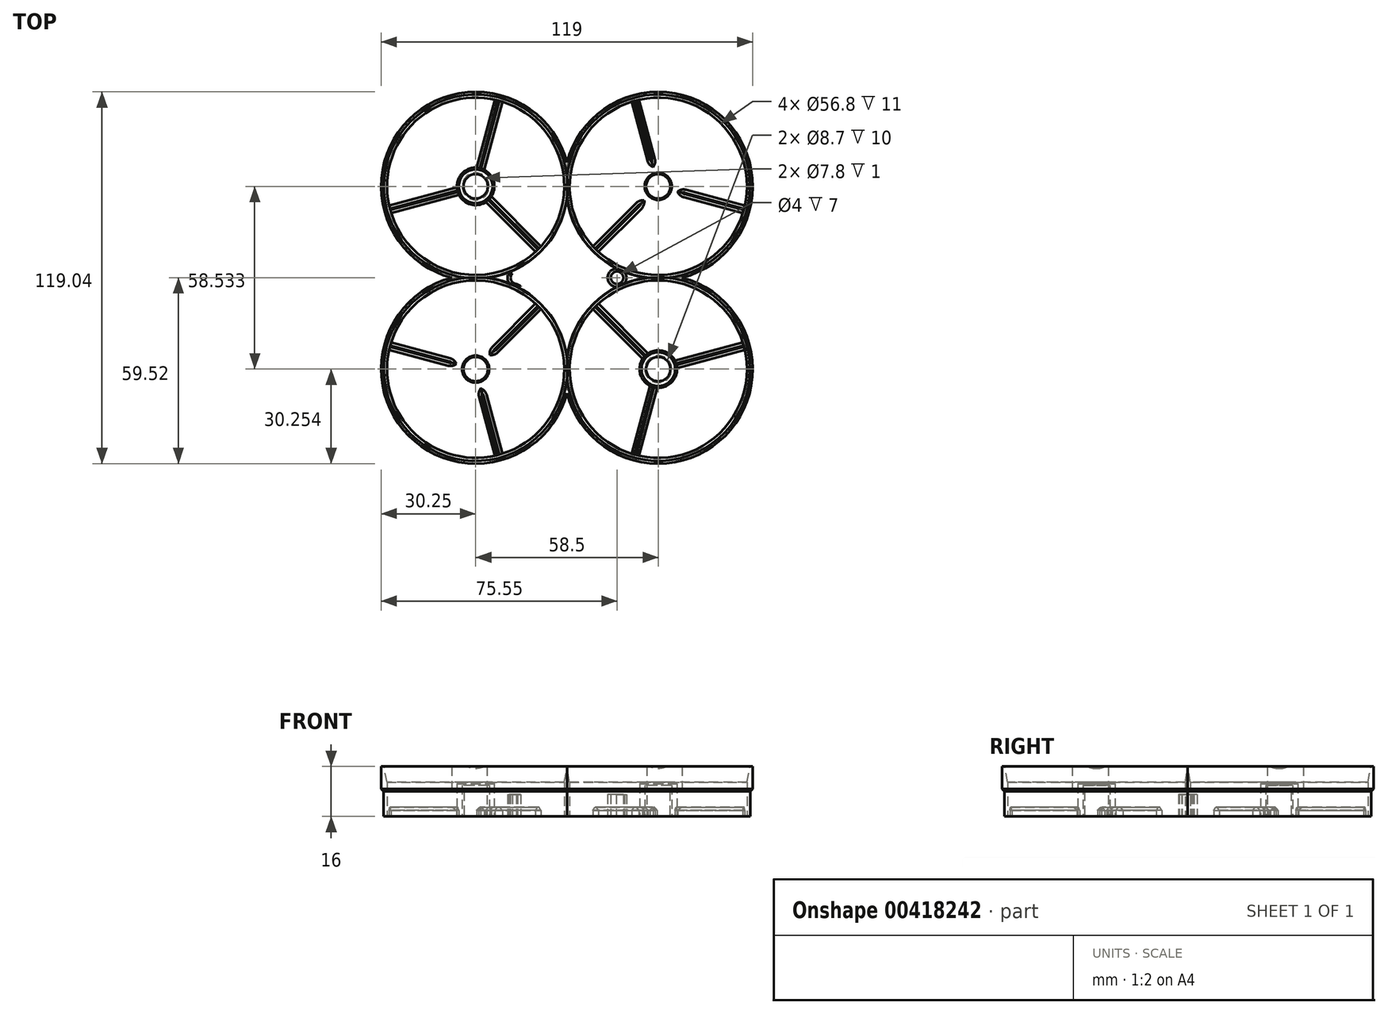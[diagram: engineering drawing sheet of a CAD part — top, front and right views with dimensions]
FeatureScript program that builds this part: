
annotation { "Feature Type Name" : "Feature", "Feature Type Description" : "" }
export const myFeature = defineFeature(function(context is Context, id is Id, definition is map)
    precondition{}
    {
        {
            var Q0;
            Q0=qCreatedBy(makeId("Top.planeOp"),FACE);
            var sketch = newSketch(context, id + "F0", { "sketchPlane" : qUnion([Q0])});
            skPoint(sketch, "E0.middle", {"position": v(0, 0) * mm});
            skCircle(sketch, "E1", {"center": v(-29.25, 29.27) * mm, "radius": 28.4 * mm});
            skArc(sketch, "E2", {"start": v(0, 33.1) * mm, "mid": v(-50.16, 50.08) * mm, "end": v(-32.96, 0) * mm});
            skArc(sketch, "E3.MirrorC", {"start": v(0, 33.1) * mm, "mid": v(50.16, 50.08) * mm, "end": v(32.96, 0) * mm});
            skCircle(sketch, "E4.MirrorC", {"center": v(29.25, 29.27) * mm, "radius": 28.4 * mm});
            skArc(sketch, "E5.MirrorC", {"start": v(0, -33.1) * mm, "mid": v(-50.16, -50.08) * mm, "end": v(-32.96, 0) * mm});
            skCircle(sketch, "E6.MirrorC", {"center": v(-29.25, -29.27) * mm, "radius": 28.4 * mm});
            skArc(sketch, "E7.MirrorC", {"start": v(0, -33.1) * mm, "mid": v(50.16, -50.08) * mm, "end": v(32.96, 0) * mm});
            skCircle(sketch, "E8.MirrorC", {"center": v(29.25, -29.27) * mm, "radius": 28.4 * mm});
            skArc(sketch, "E9.trimOffspring", {"start": v(-25.54, 0) * mm, "mid": v(-8.44, -8.36) * mm, "end": v(0, -25.43) * mm});
            skArc(sketch, "E10.trimOffspring", {"start": v(-25.54, 0) * mm, "mid": v(-8.44, 8.36) * mm, "end": v(0, 25.43) * mm});
            skArc(sketch, "E11.trimOffspring", {"start": v(25.54, 0) * mm, "mid": v(8.44, -8.36) * mm, "end": v(0, -25.43) * mm});
            skArc(sketch, "E12.trimOffspring", {"start": v(25.54, 0) * mm, "mid": v(8.44, 8.36) * mm, "end": v(0, 25.43) * mm});
            skArc(sketch, "E13", {"start": v(-21.6, 0) * mm, "mid": v(-7.88, 7.85) * mm, "end": v(0, 21.55) * mm});
            skArc(sketch, "E14.MirrorC", {"start": v(21.6, 0) * mm, "mid": v(7.88, 7.85) * mm, "end": v(0, 21.55) * mm});
            skArc(sketch, "E15.MirrorC", {"start": v(-21.6, 0) * mm, "mid": v(-7.88, -7.85) * mm, "end": v(0, -21.55) * mm});
            skArc(sketch, "E16.MirrorC", {"start": v(21.6, 0) * mm, "mid": v(7.88, -7.85) * mm, "end": v(0, -21.55) * mm});
            skArc(sketch, "E17.trimOffspring", {"start": v(0, 36.98) * mm, "mid": v(50.66, 50.63) * mm, "end": v(36.9, 0) * mm});
            skArc(sketch, "E18.trimOffspring", {"start": v(0, 36.98) * mm, "mid": v(-50.66, 50.63) * mm, "end": v(-36.9, 0) * mm});
            skArc(sketch, "E19.trimOffspring", {"start": v(0, -36.98) * mm, "mid": v(50.66, -50.63) * mm, "end": v(36.9, 0) * mm});
            skArc(sketch, "E20.trimOffspring", {"start": v(0, -36.98) * mm, "mid": v(-50.66, -50.63) * mm, "end": v(-36.9, 0) * mm});
            skLineSegment(sketch, "E21", {"start": v(-24.23, 25.98) * mm, "end": v(-8.32, 10.07) * mm});
            skLineSegment(sketch, "E22.MirrorCS", {"start": v(-25.98, 24.24) * mm, "end": v(-10.07, 8.32) * mm});
            skLineSegment(sketch, "E23.1.0", {"start": v(-28.92, 35.26) * mm, "end": v(-23.1, 57) * mm});
            skLineSegment(sketch, "E23.1.1", {"start": v(-26.54, 34.62) * mm, "end": v(-20.71, 56.35) * mm});
            skLineSegment(sketch, "E23.2.0", {"start": v(-34.6, 26.54) * mm, "end": v(-56.33, 20.72) * mm});
            skLineSegment(sketch, "E23.2.1", {"start": v(-35.24, 28.92) * mm, "end": v(-56.97, 23.1) * mm});
            skPoint(sketch, "E24.orphan", {"position": v(-23.33, 56.1) * mm});
            skPoint(sketch, "E25.orphan", {"position": v(-20.95, 55.47) * mm});
            skPoint(sketch, "E26.orphan", {"position": v(-56.1, 23.33) * mm});
            skPoint(sketch, "E27.orphan", {"position": v(-55.47, 20.95) * mm});
            skPoint(sketch, "E28.orphan", {"position": v(-8.95, 10.7) * mm});
            skPoint(sketch, "E29.orphan", {"position": v(-10.7, 8.95) * mm});
            skPoint(sketch, "E30.orphan", {"position": v(8.95, 10.7) * mm});
            skPoint(sketch, "E31.orphan", {"position": v(10.7, 8.95) * mm});
            skPoint(sketch, "E32.orphan", {"position": v(20.95, 55.47) * mm});
            skPoint(sketch, "E33.orphan", {"position": v(23.33, 56.1) * mm});
            skPoint(sketch, "E34.orphan", {"position": v(56.1, 23.33) * mm});
            skPoint(sketch, "E35.orphan", {"position": v(55.47, 20.95) * mm});
            skPoint(sketch, "E36.orphan", {"position": v(-10.7, -8.95) * mm});
            skPoint(sketch, "E37.orphan", {"position": v(-8.95, -10.7) * mm});
            skPoint(sketch, "E38.orphan", {"position": v(-55.47, -20.95) * mm});
            skPoint(sketch, "E39.orphan", {"position": v(-56.1, -23.33) * mm});
            skPoint(sketch, "E40.orphan", {"position": v(-20.95, -55.47) * mm});
            skPoint(sketch, "E41.orphan", {"position": v(-23.33, -56.1) * mm});
            skPoint(sketch, "E42.orphan", {"position": v(20.95, -55.47) * mm});
            skPoint(sketch, "E43.orphan", {"position": v(23.33, -56.1) * mm});
            skPoint(sketch, "E44.orphan", {"position": v(55.47, -20.95) * mm});
            skPoint(sketch, "E45.orphan", {"position": v(56.1, -23.33) * mm});
            skPoint(sketch, "E46.orphan", {"position": v(10.7, -8.95) * mm});
            skPoint(sketch, "E47.orphan", {"position": v(8.95, -10.7) * mm});
            skCircle(sketch, "E48", {"center": v(-29.25, 29.27) * mm, "radius": 4.35 * mm});
            skCircle(sketch, "E49", {"center": v(-29.25, 29.27) * mm, "radius": 6 * mm});
            skLineSegment(sketch, "E50.MirrorCS", {"start": v(26.54, 34.62) * mm, "end": v(20.71, 56.35) * mm});
            skLineSegment(sketch, "E51.MirrorCS", {"start": v(28.92, 35.26) * mm, "end": v(23.1, 57) * mm});
            skCircle(sketch, "E52.MirrorC", {"center": v(29.25, 29.27) * mm, "radius": 6 * mm});
            skCircle(sketch, "E53.MirrorC", {"center": v(29.25, 29.27) * mm, "radius": 4.35 * mm});
            skLineSegment(sketch, "E54.MirrorCS", {"start": v(35.24, 28.92) * mm, "end": v(56.97, 23.1) * mm});
            skLineSegment(sketch, "E55.MirrorCS", {"start": v(34.6, 26.54) * mm, "end": v(56.33, 20.72) * mm});
            skLineSegment(sketch, "E56.MirrorCS", {"start": v(24.23, 25.98) * mm, "end": v(8.32, 10.07) * mm});
            skLineSegment(sketch, "E57.MirrorCS", {"start": v(25.98, 24.24) * mm, "end": v(10.07, 8.32) * mm});
            skLineSegment(sketch, "E58.MirrorCS", {"start": v(-35.24, -28.92) * mm, "end": v(-56.97, -23.1) * mm});
            skLineSegment(sketch, "E59.MirrorCS", {"start": v(-34.6, -26.54) * mm, "end": v(-56.33, -20.72) * mm});
            skLineSegment(sketch, "E60.MirrorCS", {"start": v(-28.92, -35.26) * mm, "end": v(-23.1, -57) * mm});
            skLineSegment(sketch, "E61.MirrorCS", {"start": v(-26.54, -34.62) * mm, "end": v(-20.71, -56.35) * mm});
            skLineSegment(sketch, "E62.MirrorCS", {"start": v(-24.23, -25.98) * mm, "end": v(-8.32, -10.07) * mm});
            skLineSegment(sketch, "E63.MirrorCS", {"start": v(-25.98, -24.24) * mm, "end": v(-10.07, -8.32) * mm});
            skCircle(sketch, "E64.MirrorC", {"center": v(-29.25, -29.27) * mm, "radius": 6 * mm});
            skCircle(sketch, "E65.MirrorC", {"center": v(-29.25, -29.27) * mm, "radius": 4.35 * mm});
            skLineSegment(sketch, "E66.MirrorCS", {"start": v(25.98, -24.24) * mm, "end": v(10.07, -8.32) * mm});
            skLineSegment(sketch, "E67.MirrorCS", {"start": v(24.23, -25.98) * mm, "end": v(8.32, -10.07) * mm});
            skLineSegment(sketch, "E68.MirrorCS", {"start": v(26.54, -34.62) * mm, "end": v(20.71, -56.35) * mm});
            skLineSegment(sketch, "E69.MirrorCS", {"start": v(28.92, -35.26) * mm, "end": v(23.1, -57) * mm});
            skLineSegment(sketch, "E70.MirrorCS", {"start": v(35.24, -28.92) * mm, "end": v(56.97, -23.1) * mm});
            skLineSegment(sketch, "E71.MirrorCS", {"start": v(34.6, -26.54) * mm, "end": v(56.33, -20.72) * mm});
            skCircle(sketch, "E72.MirrorC", {"center": v(29.25, -29.27) * mm, "radius": 6 * mm});
            skCircle(sketch, "E73.MirrorC", {"center": v(29.25, -29.27) * mm, "radius": 4.35 * mm});
            skLineSegment(sketch, "E74.trimOffspring", {"start": v(-9.17, 9.18) * mm, "end": v(0, 0) * mm});
            skPoint(sketch, "E75.start.orphan", {"position": v(-26.17, 26.19) * mm});
            skPoint(sketch, "E76.trimOffspring.end.orphan", {"position": v(-25, 25.02) * mm});
            skSolve(sketch);
        }
        {
            var Q0;
            Q0=makeQuery(id+"F0.imprint","IMPRINT",FACE,{"disambiguationData":[TD([[makeQuery(id+"F0.imprint","IMPRINT",EDGE,{"derivedFrom":sQuery(id+"F0.wireOp",EDGE,"E1")}),-1.0]])]});
            extrude(context, id + "F1", {"entities" : qUnion([Q0]), "depth" : 16 * mm});
        }
        {
            var Q0;
            Q0=makeQuery(id+"F0.imprint","IMPRINT",FACE,{"disambiguationData":[TD([[makeQuery(id+"F0.imprint","IMPRINT",EDGE,{"derivedFrom":sQuery(id+"F0.wireOp",EDGE,"E2")}),-1.0]])]});
            var Q1;
            Q1=makeQuery(id+"F0.imprint","IMPRINT",FACE,{"disambiguationData":[TD([[makeQuery(id+"F0.imprint","IMPRINT",EDGE,{"derivedFrom":sQuery(id+"F0.wireOp",EDGE,"E9.trimOffspring")}),1.0]])]});
            extrude(context, id + "F2", {"entities" : qUnion([Q0, Q1]), "operationType" : NewBodyOperationType.ADD, "depth" : 16 * mm, "hasSecondDirection" : true, "secondDirectionOppositeDirection" : false, "secondDirectionDepth" : 8 * mm});
        }
        {
            var Q0;
            Q0=makeQuery(id+"F1.opExtrude","CAP_EDGE",EDGE,{"disambiguationData":[OSD([sQuery(id+"F0.wireOp",EDGE,"E1")])],"isStart":false});
            var Q1;
            Q1=makeQuery(id+"F1.opExtrude","CAP_EDGE",EDGE,{"disambiguationData":[OSD([sQuery(id+"F0.wireOp",EDGE,"E6.MirrorC")])],"isStart":false});
            var Q2;
            Q2=makeQuery(id+"F1.opExtrude","CAP_EDGE",EDGE,{"disambiguationData":[OSD([sQuery(id+"F0.wireOp",EDGE,"E4.MirrorC")])],"isStart":false});
            var Q3;
            Q3=makeQuery(id+"F1.opExtrude","CAP_EDGE",EDGE,{"disambiguationData":[OSD([sQuery(id+"F0.wireOp",EDGE,"E8.MirrorC")])],"isStart":false});
            chamfer(context, id + "F3", {"entities" : qUnion([Q0, Q1, Q2, Q3]), "chamferType" : ChamferType.TWO_OFFSETS, "width1" : 1 * mm, "oppositeDirection" : true, "width2" : 5 * mm, "tangentPropagation" : true});
        }
        {
            var Q0;
            Q0=makeQuery(id+"F0.imprint","IMPRINT",FACE,{"disambiguationData":[TD([[makeQuery(id+"F0.imprint","IMPRINT",EDGE,{"derivedFrom":sQuery(id+"F0.wireOp",EDGE,"E13")}),-1.0]])]});
            var sketch = newSketch(context, id + "F4", { "sketchPlane" : qUnion([Q0])});
            skCircle(sketch, "E77", {"center": v(16.05, 0) * mm, "radius": 3 * mm});
            skCircle(sketch, "E78", {"center": v(16.05, 0) * mm, "radius": 2 * mm});
            skCircle(sketch, "E79.2.0", {"center": v(-16.05, 0) * mm, "radius": 3 * mm});
            skCircle(sketch, "E79.2.1", {"center": v(-16.05, 0) * mm, "radius": 2 * mm});
            skPoint(sketch, "E79.center", {"position": v(0, 0) * mm});
            skSolve(sketch);
        }
        {
            var Q0;
            {var subQ0=sQuery(id+"F4.wireOp",EDGE,"E79.1.0");var subQ1=makeQuery(id+"F0.imprint","IMPRINT",EDGE,{"derivedFrom":sQuery(id+"F0.wireOp",EDGE,"E13")});var subQ2=makeQuery(id+"F4.imprint","INTERSECT",VERTEX,{"disambiguationData":[OD(0.0)],"derivedFrom":[subQ1,subQ0]});Q0=makeQuery(id+"F4.imprint","IMPRINT",FACE,{"disambiguationData":[TD([[makeQuery(id+"F4.imprint","IMPRINT",EDGE,{"disambiguationData":[TD([[subQ2,-1.0]])],"derivedFrom":subQ0}),1.0]])]});}
            var Q1;
            {var subQ0=sQuery(id+"F4.wireOp",EDGE,"E79.1.0");var subQ1=makeQuery(id+"F0.imprint","IMPRINT",EDGE,{"derivedFrom":sQuery(id+"F0.wireOp",EDGE,"E13")});var subQ2=makeQuery(id+"F4.imprint","INTERSECT",VERTEX,{"disambiguationData":[OD(1.0)],"derivedFrom":[subQ1,subQ0]});Q1=makeQuery(id+"F4.imprint","IMPRINT",FACE,{"disambiguationData":[TD([[makeQuery(id+"F4.imprint","IMPRINT",EDGE,{"disambiguationData":[TD([[subQ2,1.0]])],"derivedFrom":subQ0}),1.0]])]});}
            var Q2;
            {var subQ0=sQuery(id+"F4.wireOp",EDGE,"E79.1.0");var subQ1=makeQuery(id+"F0.imprint","IMPRINT",EDGE,{"derivedFrom":sQuery(id+"F0.wireOp",EDGE,"E13")});var subQ2=makeQuery(id+"F4.imprint","INTERSECT",VERTEX,{"disambiguationData":[OD(0.0)],"derivedFrom":[subQ1,subQ0]});Q2=makeQuery(id+"F4.imprint","IMPRINT",FACE,{"disambiguationData":[TD([[makeQuery(id+"F4.imprint","IMPRINT",EDGE,{"disambiguationData":[TD([[subQ2,1.0]])],"derivedFrom":subQ0}),1.0]])]});}
            var Q3;
            {var subQ0=sQuery(id+"F4.wireOp",EDGE,"E79.1.0");var subQ1=makeQuery(id+"F0.imprint","IMPRINT",EDGE,{"derivedFrom":sQuery(id+"F0.wireOp",EDGE,"E14.MirrorC")});var subQ2=makeQuery(id+"F4.imprint","INTERSECT",VERTEX,{"disambiguationData":[OD(0.0)],"derivedFrom":[subQ1,subQ0]});Q3=makeQuery(id+"F4.imprint","IMPRINT",FACE,{"disambiguationData":[TD([[makeQuery(id+"F4.imprint","IMPRINT",EDGE,{"disambiguationData":[TD([[subQ2,-1.0]])],"derivedFrom":subQ0}),1.0]])]});}
            var Q4;
            {var subQ0=sQuery(id+"F4.wireOp",EDGE,"E79.2.0");var subQ1=makeQuery(id+"F0.imprint","IMPRINT",EDGE,{"derivedFrom":sQuery(id+"F0.wireOp",EDGE,"E15.MirrorC")});var subQ2=makeQuery(id+"F4.imprint","INTERSECT",VERTEX,{"disambiguationData":[OD(1.0)],"derivedFrom":[subQ1,subQ0]});Q4=makeQuery(id+"F4.imprint","IMPRINT",FACE,{"disambiguationData":[TD([[makeQuery(id+"F4.imprint","IMPRINT",EDGE,{"disambiguationData":[TD([[subQ2,1.0]])],"derivedFrom":subQ0}),1.0]])]});}
            var Q5;
            {var subQ0=sQuery(id+"F4.wireOp",EDGE,"E79.2.0");var subQ1=makeQuery(id+"F0.imprint","IMPRINT",EDGE,{"derivedFrom":sQuery(id+"F0.wireOp",EDGE,"E13")});var subQ2=makeQuery(id+"F4.imprint","INTERSECT",VERTEX,{"disambiguationData":[OD(0.0)],"derivedFrom":[subQ1,subQ0]});Q5=makeQuery(id+"F4.imprint","IMPRINT",FACE,{"disambiguationData":[TD([[makeQuery(id+"F4.imprint","IMPRINT",EDGE,{"disambiguationData":[TD([[subQ2,-1.0]])],"derivedFrom":subQ0}),1.0]])]});}
            var Q6;
            {var subQ0=sQuery(id+"F4.wireOp",EDGE,"E79.2.0");var subQ1=makeQuery(id+"F0.imprint","IMPRINT",EDGE,{"derivedFrom":sQuery(id+"F0.wireOp",EDGE,"E15.MirrorC")});var subQ2=makeQuery(id+"F4.imprint","INTERSECT",VERTEX,{"disambiguationData":[OD(0.0)],"derivedFrom":[subQ1,subQ0]});Q6=makeQuery(id+"F4.imprint","IMPRINT",FACE,{"disambiguationData":[TD([[makeQuery(id+"F4.imprint","IMPRINT",EDGE,{"disambiguationData":[TD([[subQ2,1.0]])],"derivedFrom":subQ0}),1.0]])]});}
            var Q7;
            {var subQ0=sQuery(id+"F4.wireOp",EDGE,"E79.2.0");var subQ1=makeQuery(id+"F0.imprint","IMPRINT",EDGE,{"derivedFrom":sQuery(id+"F0.wireOp",EDGE,"E15.MirrorC")});var subQ2=makeQuery(id+"F4.imprint","INTERSECT",VERTEX,{"disambiguationData":[OD(0.0)],"derivedFrom":[subQ1,subQ0]});Q7=makeQuery(id+"F4.imprint","IMPRINT",FACE,{"disambiguationData":[TD([[makeQuery(id+"F4.imprint","IMPRINT",EDGE,{"disambiguationData":[TD([[subQ2,-1.0]])],"derivedFrom":subQ0}),1.0]])]});}
            var Q8;
            {var subQ0=sQuery(id+"F4.wireOp",EDGE,"E79.3.0");var subQ1=makeQuery(id+"F0.imprint","IMPRINT",EDGE,{"derivedFrom":sQuery(id+"F0.wireOp",EDGE,"E15.MirrorC")});var subQ2=makeQuery(id+"F4.imprint","INTERSECT",VERTEX,{"disambiguationData":[OD(0.0)],"derivedFrom":[subQ1,subQ0]});Q8=makeQuery(id+"F4.imprint","IMPRINT",FACE,{"disambiguationData":[TD([[makeQuery(id+"F4.imprint","IMPRINT",EDGE,{"disambiguationData":[TD([[subQ2,-1.0]])],"derivedFrom":subQ0}),1.0]])]});}
            var Q9;
            {var subQ0=sQuery(id+"F4.wireOp",EDGE,"E79.3.0");var subQ1=makeQuery(id+"F0.imprint","IMPRINT",EDGE,{"derivedFrom":sQuery(id+"F0.wireOp",EDGE,"E16.MirrorC")});var subQ2=makeQuery(id+"F4.imprint","INTERSECT",VERTEX,{"disambiguationData":[OD(0.0)],"derivedFrom":[subQ1,subQ0]});Q9=makeQuery(id+"F4.imprint","IMPRINT",FACE,{"disambiguationData":[TD([[makeQuery(id+"F4.imprint","IMPRINT",EDGE,{"disambiguationData":[TD([[subQ2,-1.0]])],"derivedFrom":subQ0}),1.0]])]});}
            var Q10;
            {var subQ0=sQuery(id+"F4.wireOp",EDGE,"E79.3.0");var subQ1=makeQuery(id+"F0.imprint","IMPRINT",EDGE,{"derivedFrom":sQuery(id+"F0.wireOp",EDGE,"E16.MirrorC")});var subQ2=makeQuery(id+"F4.imprint","INTERSECT",VERTEX,{"disambiguationData":[OD(1.0)],"derivedFrom":[subQ1,subQ0]});Q10=makeQuery(id+"F4.imprint","IMPRINT",FACE,{"disambiguationData":[TD([[makeQuery(id+"F4.imprint","IMPRINT",EDGE,{"disambiguationData":[TD([[subQ2,1.0]])],"derivedFrom":subQ0}),1.0]])]});}
            var Q11;
            {var subQ0=sQuery(id+"F4.wireOp",EDGE,"E79.3.0");var subQ1=makeQuery(id+"F0.imprint","IMPRINT",EDGE,{"derivedFrom":sQuery(id+"F0.wireOp",EDGE,"E16.MirrorC")});var subQ2=makeQuery(id+"F4.imprint","INTERSECT",VERTEX,{"disambiguationData":[OD(0.0)],"derivedFrom":[subQ1,subQ0]});Q11=makeQuery(id+"F4.imprint","IMPRINT",FACE,{"disambiguationData":[TD([[makeQuery(id+"F4.imprint","IMPRINT",EDGE,{"disambiguationData":[TD([[subQ2,1.0]])],"derivedFrom":subQ0}),1.0]])]});}
            var Q12;
            {var subQ0=sQuery(id+"F4.wireOp",EDGE,"E77");var subQ1=makeQuery(id+"F0.imprint","IMPRINT",EDGE,{"derivedFrom":sQuery(id+"F0.wireOp",EDGE,"E14.MirrorC")});var subQ2=makeQuery(id+"F4.imprint","INTERSECT",VERTEX,{"disambiguationData":[OD(0.0)],"derivedFrom":[subQ1,subQ0]});Q12=makeQuery(id+"F4.imprint","IMPRINT",FACE,{"disambiguationData":[TD([[makeQuery(id+"F4.imprint","IMPRINT",EDGE,{"disambiguationData":[TD([[subQ2,-1.0]])],"derivedFrom":subQ0}),1.0]])]});}
            var Q13;
            {var subQ0=sQuery(id+"F4.wireOp",EDGE,"E77");var subQ1=makeQuery(id+"F0.imprint","IMPRINT",EDGE,{"derivedFrom":sQuery(id+"F0.wireOp",EDGE,"E16.MirrorC")});var subQ2=makeQuery(id+"F4.imprint","INTERSECT",VERTEX,{"disambiguationData":[OD(0.0)],"derivedFrom":[subQ1,subQ0]});Q13=makeQuery(id+"F4.imprint","IMPRINT",FACE,{"disambiguationData":[TD([[makeQuery(id+"F4.imprint","IMPRINT",EDGE,{"disambiguationData":[TD([[subQ2,-1.0]])],"derivedFrom":subQ0}),1.0]])]});}
            var Q14;
            {var subQ0=sQuery(id+"F4.wireOp",EDGE,"E77");var subQ1=makeQuery(id+"F0.imprint","IMPRINT",EDGE,{"derivedFrom":sQuery(id+"F0.wireOp",EDGE,"E14.MirrorC")});var subQ2=makeQuery(id+"F4.imprint","INTERSECT",VERTEX,{"disambiguationData":[OD(0.0)],"derivedFrom":[subQ1,subQ0]});Q14=makeQuery(id+"F4.imprint","IMPRINT",FACE,{"disambiguationData":[TD([[makeQuery(id+"F4.imprint","IMPRINT",EDGE,{"disambiguationData":[TD([[subQ2,1.0]])],"derivedFrom":subQ0}),1.0]])]});}
            var Q15;
            {var subQ0=sQuery(id+"F4.wireOp",EDGE,"E77");var subQ1=makeQuery(id+"F0.imprint","IMPRINT",EDGE,{"derivedFrom":sQuery(id+"F0.wireOp",EDGE,"E14.MirrorC")});var subQ2=makeQuery(id+"F4.imprint","INTERSECT",VERTEX,{"disambiguationData":[OD(1.0)],"derivedFrom":[subQ1,subQ0]});Q15=makeQuery(id+"F4.imprint","IMPRINT",FACE,{"disambiguationData":[TD([[makeQuery(id+"F4.imprint","IMPRINT",EDGE,{"disambiguationData":[TD([[subQ2,1.0]])],"derivedFrom":subQ0}),1.0]])]});}
            extrude(context, id + "F5", {"entities" : qUnion([Q0, Q1, Q2, Q3, Q4, Q5, Q6, Q7, Q8, Q9, Q10, Q11, Q12, Q13, Q14, Q15]), "operationType" : NewBodyOperationType.ADD, "depth" : 7 * mm});
        }
        {
            var Q0;
            {var subQ0=sQuery(id+"F0.wireOp",EDGE,"E50.MirrorCS");Q0=makeQuery(id+"F0.imprint","IMPRINT",FACE,{"disambiguationData":[TD([[makeQuery(id+"F0.imprint","IMPRINT",EDGE,{"derivedFrom":subQ0}),-1.0]])]});}
            var Q1;
            {var subQ0=sQuery(id+"F0.wireOp",EDGE,"E54.MirrorCS");Q1=makeQuery(id+"F0.imprint","IMPRINT",FACE,{"disambiguationData":[TD([[makeQuery(id+"F0.imprint","IMPRINT",EDGE,{"derivedFrom":subQ0}),-1.0]])]});}
            var Q2;
            {var subQ0=sQuery(id+"F0.wireOp",EDGE,"E56.MirrorCS");Q2=makeQuery(id+"F0.imprint","IMPRINT",FACE,{"disambiguationData":[TD([[makeQuery(id+"F0.imprint","IMPRINT",EDGE,{"derivedFrom":subQ0}),1.0]])]});}
            var Q3;
            {var subQ0=sQuery(id+"F0.wireOp",EDGE,"E66.MirrorCS");Q3=makeQuery(id+"F0.imprint","IMPRINT",FACE,{"disambiguationData":[TD([[makeQuery(id+"F0.imprint","IMPRINT",EDGE,{"derivedFrom":subQ0}),1.0]])]});}
            var Q4;
            {var subQ0=sQuery(id+"F0.wireOp",EDGE,"E70.MirrorCS");Q4=makeQuery(id+"F0.imprint","IMPRINT",FACE,{"disambiguationData":[TD([[makeQuery(id+"F0.imprint","IMPRINT",EDGE,{"derivedFrom":subQ0}),1.0]])]});}
            var Q5;
            {var subQ0=sQuery(id+"F0.wireOp",EDGE,"E68.MirrorCS");Q5=makeQuery(id+"F0.imprint","IMPRINT",FACE,{"disambiguationData":[TD([[makeQuery(id+"F0.imprint","IMPRINT",EDGE,{"derivedFrom":subQ0}),1.0]])]});}
            var Q6;
            {var subQ0=sQuery(id+"F0.wireOp",EDGE,"E60.MirrorCS");Q6=makeQuery(id+"F0.imprint","IMPRINT",FACE,{"disambiguationData":[TD([[makeQuery(id+"F0.imprint","IMPRINT",EDGE,{"derivedFrom":subQ0}),1.0]])]});}
            var Q7;
            {var subQ0=sQuery(id+"F0.wireOp",EDGE,"E62.MirrorCS");Q7=makeQuery(id+"F0.imprint","IMPRINT",FACE,{"disambiguationData":[TD([[makeQuery(id+"F0.imprint","IMPRINT",EDGE,{"derivedFrom":subQ0}),1.0]])]});}
            var Q8;
            {var subQ0=sQuery(id+"F0.wireOp",EDGE,"E58.MirrorCS");Q8=makeQuery(id+"F0.imprint","IMPRINT",FACE,{"disambiguationData":[TD([[makeQuery(id+"F0.imprint","IMPRINT",EDGE,{"derivedFrom":subQ0}),-1.0]])]});}
            var Q9;
            {var subQ0=sQuery(id+"F0.wireOp",EDGE,"E23.2.0");Q9=makeQuery(id+"F0.imprint","IMPRINT",FACE,{"disambiguationData":[TD([[makeQuery(id+"F0.imprint","IMPRINT",EDGE,{"derivedFrom":subQ0}),-1.0]])]});}
            var Q10;
            {var subQ0=sQuery(id+"F0.wireOp",EDGE,"E23.1.0");Q10=makeQuery(id+"F0.imprint","IMPRINT",FACE,{"disambiguationData":[TD([[makeQuery(id+"F0.imprint","IMPRINT",EDGE,{"derivedFrom":subQ0}),-1.0]])]});}
            var Q11;
            {var subQ0=sQuery(id+"F0.wireOp",EDGE,"E21");Q11=makeQuery(id+"F0.imprint","IMPRINT",FACE,{"disambiguationData":[TD([[makeQuery(id+"F0.imprint","IMPRINT",EDGE,{"derivedFrom":subQ0}),-1.0]])]});}
            extrude(context, id + "F6", {"entities" : qUnion([Q0, Q1, Q2, Q3, Q4, Q5, Q6, Q7, Q8, Q9, Q10, Q11]), "operationType" : NewBodyOperationType.ADD, "depth" : 3 * mm});
        }
        {
            var Q0;
            Q0=makeQuery(id+"F0.imprint","IMPRINT",FACE,{"disambiguationData":[TD([[makeQuery(id+"F0.imprint","IMPRINT",EDGE,{"derivedFrom":sQuery(id+"F0.wireOp",EDGE,"E48")}),-1.0]])]});
            var Q1;
            Q1=makeQuery(id+"F0.imprint","IMPRINT",FACE,{"disambiguationData":[TD([[makeQuery(id+"F0.imprint","IMPRINT",EDGE,{"derivedFrom":sQuery(id+"F0.wireOp",EDGE,"E53.MirrorC")}),1.0]])]});
            var Q2;
            Q2=makeQuery(id+"F0.imprint","IMPRINT",FACE,{"disambiguationData":[TD([[makeQuery(id+"F0.imprint","IMPRINT",EDGE,{"derivedFrom":sQuery(id+"F0.wireOp",EDGE,"E65.MirrorC")}),1.0]])]});
            var Q3;
            Q3=makeQuery(id+"F0.imprint","IMPRINT",FACE,{"disambiguationData":[TD([[makeQuery(id+"F0.imprint","IMPRINT",EDGE,{"derivedFrom":sQuery(id+"F0.wireOp",EDGE,"E73.MirrorC")}),-1.0]])]});
            extrude(context, id + "F7", {"entities" : qUnion([Q0, Q1, Q2, Q3]), "operationType" : NewBodyOperationType.ADD, "depth" : 10 * mm});
        }
        {
            var Q0;
            Q0=makeQuery(id+"F7.opExtrude","CAP_FACE",FACE,{"disambiguationData":[OSD([sQuery(id+"F0.wireOp",EDGE,"E48"),sQuery(id+"F0.wireOp",EDGE,"E49")])],"isStart":false});
            var sketch = newSketch(context, id + "F8", { "sketchPlane" : qUnion([Q0])});
            skCircle(sketch, "E80", {"center": v(-29.25, 29.27) * mm, "radius": 3.9 * mm});
            skCircle(sketch, "E81.MirrorC", {"center": v(29.25, 29.27) * mm, "radius": 3.9 * mm});
            skCircle(sketch, "E82.MirrorC", {"center": v(-29.25, -29.27) * mm, "radius": 3.9 * mm});
            skCircle(sketch, "E83.MirrorC", {"center": v(29.25, -29.27) * mm, "radius": 3.9 * mm});
            skCircle(sketch, "E84", {"center": v(-29.25, 29.27) * mm, "radius": 6 * mm});
            skCircle(sketch, "E85.MirrorC", {"center": v(29.25, 29.27) * mm, "radius": 6 * mm});
            skCircle(sketch, "E86.MirrorC", {"center": v(-29.25, -29.27) * mm, "radius": 6 * mm});
            skCircle(sketch, "E87.MirrorC", {"center": v(29.25, -29.27) * mm, "radius": 6 * mm});
            skSolve(sketch);
        }
        {
            var Q0;
            Q0=makeQuery(id+"F8.imprint","IMPRINT",FACE,{"disambiguationData":[TD([[makeQuery(id+"F8.imprint","IMPRINT",EDGE,{"derivedFrom":sQuery(id+"F8.wireOp",EDGE,"E82.MirrorC")}),1.0]])]});
            var Q1;
            Q1=makeQuery(id+"F8.imprint","IMPRINT",FACE,{"disambiguationData":[TD([[makeQuery(id+"F8.imprint","IMPRINT",EDGE,{"derivedFrom":sQuery(id+"F8.wireOp",EDGE,"E83.MirrorC")}),-1.0]])]});
            var Q2;
            Q2=makeQuery(id+"F8.imprint","IMPRINT",FACE,{"disambiguationData":[TD([[makeQuery(id+"F8.imprint","IMPRINT",EDGE,{"derivedFrom":sQuery(id+"F8.wireOp",EDGE,"E81.MirrorC")}),1.0]])]});
            var Q3;
            Q3=makeQuery(id+"F8.imprint","IMPRINT",FACE,{"disambiguationData":[TD([[makeQuery(id+"F8.imprint","IMPRINT",EDGE,{"derivedFrom":sQuery(id+"F8.wireOp",EDGE,"E84")}),1.0]])]});
            var Q4;
            Q4=makeQuery(id+"F8.imprint","IMPRINT",FACE,{"disambiguationData":[TD([[makeQuery(id+"F8.imprint","IMPRINT",EDGE,{"derivedFrom":sQuery(id+"F8.wireOp",EDGE,"E80")}),-1.0]])]});
            extrude(context, id + "F9", {"entities" : qUnion([Q0, Q1, Q2, Q3, Q4]), "operationType" : NewBodyOperationType.ADD, "depth" : 1 * mm});
        }
        {
            var Q0;
            Q0=makeQuery(id+"F6.opExtrude","SWEPT_EDGE",EDGE,{"disambiguationData":[OSD([sQuery(id+"F0.wireOp",EDGE,"E8.MirrorC"),sQuery(id+"F0.wireOp",EDGE,"E68.MirrorCS")])]});
            var Q1;
            Q1=makeQuery(id+"F6.opExtrude","SWEPT_EDGE",EDGE,{"disambiguationData":[OSD([sQuery(id+"F0.wireOp",EDGE,"E8.MirrorC"),sQuery(id+"F0.wireOp",EDGE,"E69.MirrorCS")])]});
            var Q2;
            Q2=makeQuery(id+"F6.opExtrude","SWEPT_EDGE",EDGE,{"disambiguationData":[OSD([sQuery(id+"F0.wireOp",EDGE,"E69.MirrorCS"),sQuery(id+"F0.wireOp",EDGE,"E72.MirrorC")])]});
            var Q3;
            Q3=makeQuery(id+"F6.opExtrude","SWEPT_EDGE",EDGE,{"disambiguationData":[OSD([sQuery(id+"F0.wireOp",EDGE,"E68.MirrorCS"),sQuery(id+"F0.wireOp",EDGE,"E72.MirrorC")])]});
            var Q4;
            Q4=makeQuery(id+"F6.opExtrude","SWEPT_EDGE",EDGE,{"disambiguationData":[OSD([sQuery(id+"F0.wireOp",EDGE,"E67.MirrorCS"),sQuery(id+"F0.wireOp",EDGE,"E72.MirrorC")])]});
            var Q5;
            Q5=makeQuery(id+"F6.opExtrude","SWEPT_EDGE",EDGE,{"disambiguationData":[OSD([sQuery(id+"F0.wireOp",EDGE,"E70.MirrorCS"),sQuery(id+"F0.wireOp",EDGE,"E72.MirrorC")])]});
            var Q6;
            Q6=makeQuery(id+"F6.opExtrude","SWEPT_EDGE",EDGE,{"disambiguationData":[OSD([sQuery(id+"F0.wireOp",EDGE,"E71.MirrorCS"),sQuery(id+"F0.wireOp",EDGE,"E72.MirrorC")])]});
            var Q7;
            Q7=makeQuery(id+"F6.opExtrude","SWEPT_EDGE",EDGE,{"disambiguationData":[OSD([sQuery(id+"F0.wireOp",EDGE,"E66.MirrorCS"),sQuery(id+"F0.wireOp",EDGE,"E72.MirrorC")])]});
            var Q8;
            Q8=makeQuery(id+"F6.opExtrude","SWEPT_EDGE",EDGE,{"disambiguationData":[OSD([sQuery(id+"F0.wireOp",EDGE,"E8.MirrorC"),sQuery(id+"F0.wireOp",EDGE,"E71.MirrorCS")])]});
            var Q9;
            Q9=makeQuery(id+"F6.opExtrude","SWEPT_EDGE",EDGE,{"disambiguationData":[OSD([sQuery(id+"F0.wireOp",EDGE,"E8.MirrorC"),sQuery(id+"F0.wireOp",EDGE,"E70.MirrorCS")])]});
            var Q10;
            Q10=makeQuery(id+"F6.opExtrude","SWEPT_EDGE",EDGE,{"disambiguationData":[OSD([sQuery(id+"F0.wireOp",EDGE,"E8.MirrorC"),sQuery(id+"F0.wireOp",EDGE,"E67.MirrorCS")])]});
            var Q11;
            Q11=makeQuery(id+"F6.opExtrude","SWEPT_EDGE",EDGE,{"disambiguationData":[OSD([sQuery(id+"F0.wireOp",EDGE,"E8.MirrorC"),sQuery(id+"F0.wireOp",EDGE,"E66.MirrorCS")])]});
            var Q12;
            {var subQ0=sQuery(id+"F0.wireOp",EDGE,"E8.MirrorC");Q12=makeQuery(id+"F6.opExtrude","CAP_EDGE",EDGE,{"disambiguationData":[OSD([subQ0]),TDD([makeQuery(id+"F0.imprint","IMPRINT",EDGE,{"disambiguationData":[TD([[makeQuery(id+"F0.imprint","INTERSECT",VERTEX,{"derivedFrom":[subQ0,sQuery(id+"F0.wireOp",EDGE,"E66.MirrorCS")]}),-1.0]])],"derivedFrom":subQ0})])],"isStart":false});}
            var Q13;
            {var subQ0=sQuery(id+"F0.wireOp",EDGE,"E8.MirrorC");Q13=makeQuery(id+"F6.opExtrude","CAP_EDGE",EDGE,{"disambiguationData":[OSD([subQ0]),TDD([makeQuery(id+"F0.imprint","IMPRINT",EDGE,{"disambiguationData":[TD([[makeQuery(id+"F0.imprint","INTERSECT",VERTEX,{"derivedFrom":[subQ0,sQuery(id+"F0.wireOp",EDGE,"E70.MirrorCS")]}),-1.0]])],"derivedFrom":subQ0})])],"isStart":false});}
            var Q14;
            {var subQ0=sQuery(id+"F0.wireOp",EDGE,"E8.MirrorC");Q14=makeQuery(id+"F6.opExtrude","CAP_EDGE",EDGE,{"disambiguationData":[OSD([subQ0]),TDD([makeQuery(id+"F0.imprint","IMPRINT",EDGE,{"disambiguationData":[TD([[makeQuery(id+"F0.imprint","INTERSECT",VERTEX,{"derivedFrom":[subQ0,sQuery(id+"F0.wireOp",EDGE,"E68.MirrorCS")]}),-1.0]])],"derivedFrom":subQ0})])],"isStart":false});}
            var Q15;
            {var subQ0=sQuery(id+"F0.wireOp",EDGE,"E72.MirrorC");Q15=makeQuery(id+"F6.opExtrude","CAP_EDGE",EDGE,{"disambiguationData":[OSD([subQ0]),TDD([makeQuery(id+"F0.imprint","IMPRINT",EDGE,{"disambiguationData":[TD([[makeQuery(id+"F0.imprint","INTERSECT",VERTEX,{"derivedFrom":[sQuery(id+"F0.wireOp",EDGE,"E68.MirrorCS"),subQ0]}),-1.0]])],"derivedFrom":subQ0})])],"isStart":false});}
            var Q16;
            {var subQ0=sQuery(id+"F0.wireOp",EDGE,"E72.MirrorC");Q16=makeQuery(id+"F6.opExtrude","CAP_EDGE",EDGE,{"disambiguationData":[OSD([subQ0]),TDD([makeQuery(id+"F0.imprint","IMPRINT",EDGE,{"disambiguationData":[TD([[makeQuery(id+"F0.imprint","INTERSECT",VERTEX,{"derivedFrom":[sQuery(id+"F0.wireOp",EDGE,"E70.MirrorCS"),subQ0]}),-1.0]])],"derivedFrom":subQ0})])],"isStart":false});}
            var Q17;
            {var subQ0=sQuery(id+"F0.wireOp",EDGE,"E72.MirrorC");Q17=makeQuery(id+"F6.opExtrude","CAP_EDGE",EDGE,{"disambiguationData":[OSD([subQ0]),TDD([makeQuery(id+"F0.imprint","IMPRINT",EDGE,{"disambiguationData":[TD([[makeQuery(id+"F0.imprint","INTERSECT",VERTEX,{"derivedFrom":[sQuery(id+"F0.wireOp",EDGE,"E66.MirrorCS"),subQ0]}),-1.0]])],"derivedFrom":subQ0})])],"isStart":false});}
            var Q18;
            {var subQ0=sQuery(id+"F0.wireOp",EDGE,"E4.MirrorC");Q18=makeQuery(id+"F6.opExtrude","CAP_EDGE",EDGE,{"disambiguationData":[OSD([subQ0]),TDD([makeQuery(id+"F0.imprint","IMPRINT",EDGE,{"disambiguationData":[TD([[makeQuery(id+"F0.imprint","INTERSECT",VERTEX,{"derivedFrom":[subQ0,sQuery(id+"F0.wireOp",EDGE,"E50.MirrorCS")]}),-1.0]])],"derivedFrom":subQ0})])],"isStart":false});}
            var Q19;
            Q19=makeQuery(id+"F6.opExtrude","SWEPT_EDGE",EDGE,{"disambiguationData":[OSD([sQuery(id+"F0.wireOp",EDGE,"E4.MirrorC"),sQuery(id+"F0.wireOp",EDGE,"E51.MirrorCS")])]});
            var Q20;
            Q20=makeQuery(id+"F6.opExtrude","SWEPT_EDGE",EDGE,{"disambiguationData":[OSD([sQuery(id+"F0.wireOp",EDGE,"E4.MirrorC"),sQuery(id+"F0.wireOp",EDGE,"E50.MirrorCS")])]});
            var Q21;
            {var subQ0=sQuery(id+"F0.wireOp",EDGE,"E52.MirrorC");Q21=makeQuery(id+"F6.opExtrude","CAP_EDGE",EDGE,{"disambiguationData":[OSD([subQ0]),TDD([makeQuery(id+"F0.imprint","IMPRINT",EDGE,{"disambiguationData":[TD([[makeQuery(id+"F0.imprint","INTERSECT",VERTEX,{"derivedFrom":[subQ0,sQuery(id+"F0.wireOp",EDGE,"E56.MirrorCS")]}),1.0]])],"derivedFrom":subQ0})])],"isStart":false});}
            var Q22;
            Q22=makeQuery(id+"F6.opExtrude","SWEPT_EDGE",EDGE,{"disambiguationData":[OSD([sQuery(id+"F0.wireOp",EDGE,"E52.MirrorC"),sQuery(id+"F0.wireOp",EDGE,"E57.MirrorCS")])]});
            var Q23;
            Q23=makeQuery(id+"F6.opExtrude","SWEPT_EDGE",EDGE,{"disambiguationData":[OSD([sQuery(id+"F0.wireOp",EDGE,"E52.MirrorC"),sQuery(id+"F0.wireOp",EDGE,"E55.MirrorCS")])]});
            var Q24;
            Q24=makeQuery(id+"F6.opExtrude","SWEPT_EDGE",EDGE,{"disambiguationData":[OSD([sQuery(id+"F0.wireOp",EDGE,"E52.MirrorC"),sQuery(id+"F0.wireOp",EDGE,"E56.MirrorCS")])]});
            var Q25;
            Q25=makeQuery(id+"F6.opExtrude","SWEPT_EDGE",EDGE,{"disambiguationData":[OSD([sQuery(id+"F0.wireOp",EDGE,"E50.MirrorCS"),sQuery(id+"F0.wireOp",EDGE,"E52.MirrorC")])]});
            var Q26;
            {var subQ0=sQuery(id+"F0.wireOp",EDGE,"E52.MirrorC");Q26=makeQuery(id+"F6.opExtrude","CAP_EDGE",EDGE,{"disambiguationData":[OSD([subQ0]),TDD([makeQuery(id+"F0.imprint","IMPRINT",EDGE,{"disambiguationData":[TD([[makeQuery(id+"F0.imprint","INTERSECT",VERTEX,{"derivedFrom":[sQuery(id+"F0.wireOp",EDGE,"E50.MirrorCS"),subQ0]}),-1.0]])],"derivedFrom":subQ0})])],"isStart":false});}
            var Q27;
            Q27=makeQuery(id+"F6.opExtrude","SWEPT_EDGE",EDGE,{"disambiguationData":[OSD([sQuery(id+"F0.wireOp",EDGE,"E52.MirrorC"),sQuery(id+"F0.wireOp",EDGE,"E54.MirrorCS")])]});
            var Q28;
            Q28=makeQuery(id+"F6.opExtrude","SWEPT_EDGE",EDGE,{"disambiguationData":[OSD([sQuery(id+"F0.wireOp",EDGE,"E51.MirrorCS"),sQuery(id+"F0.wireOp",EDGE,"E52.MirrorC")])]});
            var Q29;
            {var subQ0=sQuery(id+"F0.wireOp",EDGE,"E4.MirrorC");Q29=makeQuery(id+"F6.opExtrude","CAP_EDGE",EDGE,{"disambiguationData":[OSD([subQ0]),TDD([makeQuery(id+"F0.imprint","IMPRINT",EDGE,{"disambiguationData":[TD([[makeQuery(id+"F0.imprint","INTERSECT",VERTEX,{"derivedFrom":[subQ0,sQuery(id+"F0.wireOp",EDGE,"E56.MirrorCS")]}),1.0]])],"derivedFrom":subQ0})])],"isStart":false});}
            var Q30;
            Q30=makeQuery(id+"F6.opExtrude","SWEPT_EDGE",EDGE,{"disambiguationData":[OSD([sQuery(id+"F0.wireOp",EDGE,"E4.MirrorC"),sQuery(id+"F0.wireOp",EDGE,"E56.MirrorCS")])]});
            var Q31;
            Q31=makeQuery(id+"F6.opExtrude","SWEPT_EDGE",EDGE,{"disambiguationData":[OSD([sQuery(id+"F0.wireOp",EDGE,"E4.MirrorC"),sQuery(id+"F0.wireOp",EDGE,"E57.MirrorCS")])]});
            var Q32;
            {var subQ0=sQuery(id+"F0.wireOp",EDGE,"E4.MirrorC");Q32=makeQuery(id+"F6.opExtrude","CAP_EDGE",EDGE,{"disambiguationData":[OSD([subQ0]),TDD([makeQuery(id+"F0.imprint","IMPRINT",EDGE,{"disambiguationData":[TD([[makeQuery(id+"F0.imprint","INTERSECT",VERTEX,{"derivedFrom":[subQ0,sQuery(id+"F0.wireOp",EDGE,"E54.MirrorCS")]}),-1.0]])],"derivedFrom":subQ0})])],"isStart":false});}
            var Q33;
            {var subQ0=sQuery(id+"F0.wireOp",EDGE,"E52.MirrorC");Q33=makeQuery(id+"F6.opExtrude","CAP_EDGE",EDGE,{"disambiguationData":[OSD([subQ0]),TDD([makeQuery(id+"F0.imprint","IMPRINT",EDGE,{"disambiguationData":[TD([[makeQuery(id+"F0.imprint","INTERSECT",VERTEX,{"derivedFrom":[subQ0,sQuery(id+"F0.wireOp",EDGE,"E54.MirrorCS")]}),-1.0]])],"derivedFrom":subQ0})])],"isStart":false});}
            var Q34;
            Q34=makeQuery(id+"F6.opExtrude","SWEPT_EDGE",EDGE,{"disambiguationData":[OSD([sQuery(id+"F0.wireOp",EDGE,"E4.MirrorC"),sQuery(id+"F0.wireOp",EDGE,"E54.MirrorCS")])]});
            var Q35;
            Q35=makeQuery(id+"F6.opExtrude","SWEPT_EDGE",EDGE,{"disambiguationData":[OSD([sQuery(id+"F0.wireOp",EDGE,"E4.MirrorC"),sQuery(id+"F0.wireOp",EDGE,"E55.MirrorCS")])]});
            var Q36;
            {var subQ0=sQuery(id+"F0.wireOp",EDGE,"E1");Q36=makeQuery(id+"F6.opExtrude","CAP_EDGE",EDGE,{"disambiguationData":[OSD([subQ0]),TDD([makeQuery(id+"F0.imprint","IMPRINT",EDGE,{"disambiguationData":[TD([[makeQuery(id+"F0.imprint","INTERSECT",VERTEX,{"derivedFrom":[subQ0,sQuery(id+"F0.wireOp",EDGE,"E23.1.0")]}),1.0]])],"derivedFrom":subQ0})])],"isStart":false});}
            var Q37;
            Q37=makeQuery(id+"F6.opExtrude","SWEPT_EDGE",EDGE,{"disambiguationData":[OSD([sQuery(id+"F0.wireOp",EDGE,"E1"),sQuery(id+"F0.wireOp",EDGE,"E23.1.0")])]});
            var Q38;
            Q38=makeQuery(id+"F6.opExtrude","SWEPT_EDGE",EDGE,{"disambiguationData":[OSD([sQuery(id+"F0.wireOp",EDGE,"E23.2.1"),sQuery(id+"F0.wireOp",EDGE,"E49")])]});
            var Q39;
            Q39=makeQuery(id+"F6.opExtrude","SWEPT_EDGE",EDGE,{"disambiguationData":[OSD([sQuery(id+"F0.wireOp",EDGE,"E1"),sQuery(id+"F0.wireOp",EDGE,"E23.2.1")])]});
            var Q40;
            {var subQ0=sQuery(id+"F0.wireOp",EDGE,"E1");Q40=makeQuery(id+"F6.opExtrude","CAP_EDGE",EDGE,{"disambiguationData":[OSD([subQ0]),TDD([makeQuery(id+"F0.imprint","IMPRINT",EDGE,{"disambiguationData":[TD([[makeQuery(id+"F0.imprint","INTERSECT",VERTEX,{"derivedFrom":[subQ0,sQuery(id+"F0.wireOp",EDGE,"E23.2.0")]}),1.0]])],"derivedFrom":subQ0})])],"isStart":false});}
            var Q41;
            {var subQ0=sQuery(id+"F0.wireOp",EDGE,"E49");Q41=makeQuery(id+"F6.opExtrude","CAP_EDGE",EDGE,{"disambiguationData":[OSD([subQ0]),TDD([makeQuery(id+"F0.imprint","IMPRINT",EDGE,{"disambiguationData":[TD([[makeQuery(id+"F0.imprint","INTERSECT",VERTEX,{"derivedFrom":[sQuery(id+"F0.wireOp",EDGE,"E23.1.0"),subQ0]}),1.0]])],"derivedFrom":subQ0})])],"isStart":false});}
            var Q42;
            Q42=makeQuery(id+"F6.opExtrude","SWEPT_EDGE",EDGE,{"disambiguationData":[OSD([sQuery(id+"F0.wireOp",EDGE,"E23.1.0"),sQuery(id+"F0.wireOp",EDGE,"E49")])]});
            var Q43;
            {var subQ0=sQuery(id+"F0.wireOp",EDGE,"E49");Q43=makeQuery(id+"F6.opExtrude","CAP_EDGE",EDGE,{"disambiguationData":[OSD([subQ0]),TDD([makeQuery(id+"F0.imprint","IMPRINT",EDGE,{"disambiguationData":[TD([[makeQuery(id+"F0.imprint","INTERSECT",VERTEX,{"derivedFrom":[sQuery(id+"F0.wireOp",EDGE,"E23.2.0"),subQ0]}),1.0]])],"derivedFrom":subQ0})])],"isStart":false});}
            var Q44;
            Q44=makeQuery(id+"F6.opExtrude","SWEPT_EDGE",EDGE,{"disambiguationData":[OSD([sQuery(id+"F0.wireOp",EDGE,"E23.1.1"),sQuery(id+"F0.wireOp",EDGE,"E49")])]});
            var Q45;
            {var subQ0=sQuery(id+"F0.wireOp",EDGE,"E49");Q45=makeQuery(id+"F6.opExtrude","CAP_EDGE",EDGE,{"disambiguationData":[OSD([subQ0]),TDD([makeQuery(id+"F0.imprint","IMPRINT",EDGE,{"disambiguationData":[TD([[makeQuery(id+"F0.imprint","INTERSECT",VERTEX,{"derivedFrom":[sQuery(id+"F0.wireOp",EDGE,"E21"),subQ0]}),1.0]])],"derivedFrom":subQ0})])],"isStart":false});}
            var Q46;
            Q46=makeQuery(id+"F6.opExtrude","SWEPT_EDGE",EDGE,{"disambiguationData":[OSD([sQuery(id+"F0.wireOp",EDGE,"E23.2.0"),sQuery(id+"F0.wireOp",EDGE,"E49")])]});
            var Q47;
            Q47=makeQuery(id+"F6.opExtrude","SWEPT_EDGE",EDGE,{"disambiguationData":[OSD([sQuery(id+"F0.wireOp",EDGE,"E1"),sQuery(id+"F0.wireOp",EDGE,"E23.2.0")])]});
            var Q48;
            Q48=makeQuery(id+"F6.opExtrude","SWEPT_EDGE",EDGE,{"disambiguationData":[OSD([sQuery(id+"F0.wireOp",EDGE,"E22.MirrorCS"),sQuery(id+"F0.wireOp",EDGE,"E49")])]});
            var Q49;
            Q49=makeQuery(id+"F6.opExtrude","SWEPT_EDGE",EDGE,{"disambiguationData":[OSD([sQuery(id+"F0.wireOp",EDGE,"E21"),sQuery(id+"F0.wireOp",EDGE,"E49")])]});
            var Q50;
            Q50=makeQuery(id+"F6.opExtrude","SWEPT_EDGE",EDGE,{"disambiguationData":[OSD([sQuery(id+"F0.wireOp",EDGE,"E1"),sQuery(id+"F0.wireOp",EDGE,"E21")])]});
            var Q51;
            {var subQ0=sQuery(id+"F0.wireOp",EDGE,"E1");Q51=makeQuery(id+"F6.opExtrude","CAP_EDGE",EDGE,{"disambiguationData":[OSD([subQ0]),TDD([makeQuery(id+"F0.imprint","IMPRINT",EDGE,{"disambiguationData":[TD([[makeQuery(id+"F0.imprint","INTERSECT",VERTEX,{"derivedFrom":[subQ0,sQuery(id+"F0.wireOp",EDGE,"E21")]}),1.0]])],"derivedFrom":subQ0})])],"isStart":false});}
            var Q52;
            Q52=makeQuery(id+"F6.opExtrude","SWEPT_EDGE",EDGE,{"disambiguationData":[OSD([sQuery(id+"F0.wireOp",EDGE,"E1"),sQuery(id+"F0.wireOp",EDGE,"E22.MirrorCS")])]});
            var Q53;
            Q53=makeQuery(id+"F6.opExtrude","SWEPT_EDGE",EDGE,{"disambiguationData":[OSD([sQuery(id+"F0.wireOp",EDGE,"E1"),sQuery(id+"F0.wireOp",EDGE,"E23.1.1")])]});
            var Q54;
            {var subQ0=sQuery(id+"F0.wireOp",EDGE,"E6.MirrorC");Q54=makeQuery(id+"F6.opExtrude","CAP_EDGE",EDGE,{"disambiguationData":[OSD([subQ0]),TDD([makeQuery(id+"F0.imprint","IMPRINT",EDGE,{"disambiguationData":[TD([[makeQuery(id+"F0.imprint","INTERSECT",VERTEX,{"derivedFrom":[subQ0,sQuery(id+"F0.wireOp",EDGE,"E62.MirrorCS")]}),1.0]])],"derivedFrom":subQ0})])],"isStart":false});}
            var Q55;
            Q55=makeQuery(id+"F6.opExtrude","SWEPT_EDGE",EDGE,{"disambiguationData":[OSD([sQuery(id+"F0.wireOp",EDGE,"E6.MirrorC"),sQuery(id+"F0.wireOp",EDGE,"E63.MirrorCS")])]});
            var Q56;
            Q56=makeQuery(id+"F6.opExtrude","SWEPT_EDGE",EDGE,{"disambiguationData":[OSD([sQuery(id+"F0.wireOp",EDGE,"E6.MirrorC"),sQuery(id+"F0.wireOp",EDGE,"E62.MirrorCS")])]});
            var Q57;
            {var subQ0=sQuery(id+"F0.wireOp",EDGE,"E6.MirrorC");Q57=makeQuery(id+"F6.opExtrude","CAP_EDGE",EDGE,{"disambiguationData":[OSD([subQ0]),TDD([makeQuery(id+"F0.imprint","IMPRINT",EDGE,{"disambiguationData":[TD([[makeQuery(id+"F0.imprint","INTERSECT",VERTEX,{"derivedFrom":[subQ0,sQuery(id+"F0.wireOp",EDGE,"E60.MirrorCS")]}),1.0]])],"derivedFrom":subQ0})])],"isStart":false});}
            var Q58;
            Q58=makeQuery(id+"F6.opExtrude","SWEPT_EDGE",EDGE,{"disambiguationData":[OSD([sQuery(id+"F0.wireOp",EDGE,"E6.MirrorC"),sQuery(id+"F0.wireOp",EDGE,"E60.MirrorCS")])]});
            var Q59;
            {var subQ0=sQuery(id+"F0.wireOp",EDGE,"E64.MirrorC");Q59=makeQuery(id+"F6.opExtrude","CAP_EDGE",EDGE,{"disambiguationData":[OSD([subQ0]),TDD([makeQuery(id+"F0.imprint","IMPRINT",EDGE,{"disambiguationData":[TD([[makeQuery(id+"F0.imprint","INTERSECT",VERTEX,{"derivedFrom":[sQuery(id+"F0.wireOp",EDGE,"E58.MirrorCS"),subQ0]}),-1.0]])],"derivedFrom":subQ0})])],"isStart":false});}
            var Q60;
            Q60=makeQuery(id+"F6.opExtrude","SWEPT_EDGE",EDGE,{"disambiguationData":[OSD([sQuery(id+"F0.wireOp",EDGE,"E58.MirrorCS"),sQuery(id+"F0.wireOp",EDGE,"E64.MirrorC")])]});
            var Q61;
            Q61=makeQuery(id+"F6.opExtrude","SWEPT_EDGE",EDGE,{"disambiguationData":[OSD([sQuery(id+"F0.wireOp",EDGE,"E60.MirrorCS"),sQuery(id+"F0.wireOp",EDGE,"E64.MirrorC")])]});
            var Q62;
            Q62=makeQuery(id+"F6.opExtrude","SWEPT_EDGE",EDGE,{"disambiguationData":[OSD([sQuery(id+"F0.wireOp",EDGE,"E61.MirrorCS"),sQuery(id+"F0.wireOp",EDGE,"E64.MirrorC")])]});
            var Q63;
            Q63=makeQuery(id+"F6.opExtrude","SWEPT_EDGE",EDGE,{"disambiguationData":[OSD([sQuery(id+"F0.wireOp",EDGE,"E62.MirrorCS"),sQuery(id+"F0.wireOp",EDGE,"E64.MirrorC")])]});
            var Q64;
            Q64=makeQuery(id+"F6.opExtrude","SWEPT_EDGE",EDGE,{"disambiguationData":[OSD([sQuery(id+"F0.wireOp",EDGE,"E6.MirrorC"),sQuery(id+"F0.wireOp",EDGE,"E58.MirrorCS")])]});
            var Q65;
            {var subQ0=sQuery(id+"F0.wireOp",EDGE,"E6.MirrorC");Q65=makeQuery(id+"F6.opExtrude","CAP_EDGE",EDGE,{"disambiguationData":[OSD([subQ0]),TDD([makeQuery(id+"F0.imprint","IMPRINT",EDGE,{"disambiguationData":[TD([[makeQuery(id+"F0.imprint","INTERSECT",VERTEX,{"derivedFrom":[subQ0,sQuery(id+"F0.wireOp",EDGE,"E58.MirrorCS")]}),-1.0]])],"derivedFrom":subQ0})])],"isStart":false});}
            var Q66;
            Q66=makeQuery(id+"F6.opExtrude","SWEPT_EDGE",EDGE,{"disambiguationData":[OSD([sQuery(id+"F0.wireOp",EDGE,"E6.MirrorC"),sQuery(id+"F0.wireOp",EDGE,"E59.MirrorCS")])]});
            var Q67;
            Q67=makeQuery(id+"F6.opExtrude","SWEPT_EDGE",EDGE,{"disambiguationData":[OSD([sQuery(id+"F0.wireOp",EDGE,"E59.MirrorCS"),sQuery(id+"F0.wireOp",EDGE,"E64.MirrorC")])]});
            var Q68;
            {var subQ0=sQuery(id+"F0.wireOp",EDGE,"E64.MirrorC");Q68=makeQuery(id+"F6.opExtrude","CAP_EDGE",EDGE,{"disambiguationData":[OSD([subQ0]),TDD([makeQuery(id+"F0.imprint","IMPRINT",EDGE,{"disambiguationData":[TD([[makeQuery(id+"F0.imprint","INTERSECT",VERTEX,{"derivedFrom":[sQuery(id+"F0.wireOp",EDGE,"E62.MirrorCS"),subQ0]}),1.0]])],"derivedFrom":subQ0})])],"isStart":false});}
            var Q69;
            Q69=makeQuery(id+"F6.opExtrude","SWEPT_EDGE",EDGE,{"disambiguationData":[OSD([sQuery(id+"F0.wireOp",EDGE,"E63.MirrorCS"),sQuery(id+"F0.wireOp",EDGE,"E64.MirrorC")])]});
            var Q70;
            {var subQ0=sQuery(id+"F0.wireOp",EDGE,"E64.MirrorC");Q70=makeQuery(id+"F6.opExtrude","CAP_EDGE",EDGE,{"disambiguationData":[OSD([subQ0]),TDD([makeQuery(id+"F0.imprint","IMPRINT",EDGE,{"disambiguationData":[TD([[makeQuery(id+"F0.imprint","INTERSECT",VERTEX,{"derivedFrom":[sQuery(id+"F0.wireOp",EDGE,"E60.MirrorCS"),subQ0]}),1.0]])],"derivedFrom":subQ0})])],"isStart":false});}
            var Q71;
            Q71=makeQuery(id+"F6.opExtrude","SWEPT_EDGE",EDGE,{"disambiguationData":[OSD([sQuery(id+"F0.wireOp",EDGE,"E6.MirrorC"),sQuery(id+"F0.wireOp",EDGE,"E61.MirrorCS")])]});
            fillet(context, id + "F10", {"entities" : qUnion([Q0, Q1, Q2, Q3, Q4, Q5, Q6, Q7, Q8, Q9, Q10, Q11, Q12, Q13, Q14, Q15, Q16, Q17, Q18, Q19, Q20, Q21, Q22, Q23, Q24, Q25, Q26, Q27, Q28, Q29, Q30, Q31, Q32, Q33, Q34, Q35, Q36, Q37, Q38, Q39, Q40, Q41, Q42, Q43, Q44, Q45, Q46, Q47, Q48, Q49, Q50, Q51, Q52, Q53, Q54, Q55, Q56, Q57, Q58, Q59, Q60, Q61, Q62, Q63, Q64, Q65, Q66, Q67, Q68, Q69, Q70, Q71]), "radius" : 3 * mm, "tangentPropagation" : true, "allowEdgeOverflow" : false});
        }
        {
            var Q0;
            Q0=makeQuery(id+"F2.opExtrude","CAP_EDGE",EDGE,{"disambiguationData":[OSD([sQuery(id+"F0.wireOp",EDGE,"E17.trimOffspring")])],"isStart":true});
            var Q1;
            Q1=makeQuery(id+"F2.opExtrude","CAP_EDGE",EDGE,{"disambiguationData":[OSD([sQuery(id+"F0.wireOp",EDGE,"E18.trimOffspring")])],"isStart":true});
            var Q2;
            Q2=makeQuery(id+"F2.opExtrude","CAP_EDGE",EDGE,{"disambiguationData":[OSD([sQuery(id+"F0.wireOp",EDGE,"E20.trimOffspring")])],"isStart":true});
            var Q3;
            Q3=makeQuery(id+"F2.opExtrude","CAP_EDGE",EDGE,{"disambiguationData":[OSD([sQuery(id+"F0.wireOp",EDGE,"E19.trimOffspring")])],"isStart":true});
            var Q4;
            Q4=makeQuery(id+"F2.opExtrude","CAP_EDGE",EDGE,{"disambiguationData":[OSD([sQuery(id+"F0.wireOp",EDGE,"E16.MirrorC")])],"isStart":true});
            var Q5;
            Q5=makeQuery(id+"F2.opExtrude","CAP_EDGE",EDGE,{"disambiguationData":[OSD([sQuery(id+"F0.wireOp",EDGE,"E14.MirrorC")])],"isStart":true});
            var Q6;
            Q6=makeQuery(id+"F2.opExtrude","CAP_EDGE",EDGE,{"disambiguationData":[OSD([sQuery(id+"F0.wireOp",EDGE,"E15.MirrorC")])],"isStart":true});
            var Q7;
            Q7=makeQuery(id+"F2.opExtrude","CAP_EDGE",EDGE,{"disambiguationData":[OSD([sQuery(id+"F0.wireOp",EDGE,"E13")])],"isStart":true});
            chamfer(context, id + "F11", {"entities" : qUnion([Q0, Q1, Q2, Q3, Q4, Q5, Q6, Q7]), "width" : 0.8 * mm, "tangentPropagation" : true});
        }
        {
            var Q0;
            {var subQ0=sQuery(id+"F4.wireOp",EDGE,"E79.2.0");var subQ1=sQuery(id+"F0.wireOp",EDGE,"E13");var subQ2=makeQuery(id+"F0.imprint","IMPRINT",EDGE,{"disambiguationData":[TD([[makeQuery(id+"F0.imprint","IMPRINT",VERTEX,{"derivedFrom":subQ1}),1.0]])],"derivedFrom":subQ1});var subQ3=makeQuery(id+"F4.imprint","INTERSECT",VERTEX,{"disambiguationData":[OD(0.0)],"derivedFrom":[subQ2,subQ0]});Q0=makeQuery(id+"F4.imprint","IMPRINT",FACE,{"disambiguationData":[TD([[makeQuery(id+"F4.imprint","IMPRINT",EDGE,{"disambiguationData":[TD([[subQ3,-1.0]])],"derivedFrom":subQ0}),1.0]])]});}
            var Q1;
            Q1=makeQuery(id+"F5.opExtrude","CAP_FACE",FACE,{"disambiguationData":[OSD([sQuery(id+"F0.wireOp",EDGE,"E13"),sQuery(id+"F4.wireOp",EDGE,"E79.2.0"),sQuery(id+"F4.wireOp",EDGE,"E79.2.1")])],"isStart":false});
            extrude(context, id + "F12", {"entities" : qUnion([Q0]), "operationType" : NewBodyOperationType.ADD, "endBound" : BoundingType.UP_TO_SURFACE, "endBoundEntityFace" : qUnion([Q1]), "depth" : 25 * mm});
        }
        {
            var Q0;
            Q0=makeQuery(id+"F9.opExtrude","CAP_EDGE",EDGE,{"disambiguationData":[OSD([sQuery(id+"F8.wireOp",EDGE,"E87.MirrorC")])],"isStart":false});
            var Q1;
            Q1=makeQuery(id+"F9.opExtrude","CAP_EDGE",EDGE,{"disambiguationData":[OSD([sQuery(id+"F8.wireOp",EDGE,"E85.MirrorC")])],"isStart":false});
            var Q2;
            Q2=makeQuery(id+"F9.opExtrude","CAP_EDGE",EDGE,{"disambiguationData":[OSD([sQuery(id+"F8.wireOp",EDGE,"E86.MirrorC")])],"isStart":false});
            var Q3;
            Q3=makeQuery(id+"F9.opExtrude","CAP_EDGE",EDGE,{"disambiguationData":[OSD([sQuery(id+"F8.wireOp",EDGE,"E84")])],"isStart":false});
            chamfer(context, id + "F13", {"entities" : qUnion([Q0, Q1, Q2, Q3]), "width" : 0.6 * mm, "tangentPropagation" : true});
        }
        {
            var Q0;
            Q0=makeQuery(id+"F6.opExtrude","CAP_EDGE",EDGE,{"disambiguationData":[OSD([sQuery(id+"F0.wireOp",EDGE,"E58.MirrorCS")])],"isStart":false});
            var Q1;
            Q1=makeQuery(id+"F6.opExtrude","CAP_EDGE",EDGE,{"disambiguationData":[OSD([sQuery(id+"F0.wireOp",EDGE,"E59.MirrorCS")])],"isStart":false});
            var Q2;
            Q2=makeQuery(id+"F6.opExtrude","CAP_EDGE",EDGE,{"disambiguationData":[OSD([sQuery(id+"F0.wireOp",EDGE,"E62.MirrorCS")])],"isStart":false});
            var Q3;
            Q3=makeQuery(id+"F6.opExtrude","CAP_EDGE",EDGE,{"disambiguationData":[OSD([sQuery(id+"F0.wireOp",EDGE,"E63.MirrorCS")])],"isStart":false});
            var Q4;
            Q4=makeQuery(id+"F6.opExtrude","CAP_EDGE",EDGE,{"disambiguationData":[OSD([sQuery(id+"F0.wireOp",EDGE,"E61.MirrorCS")])],"isStart":false});
            var Q5;
            Q5=makeQuery(id+"F6.opExtrude","CAP_EDGE",EDGE,{"disambiguationData":[OSD([sQuery(id+"F0.wireOp",EDGE,"E60.MirrorCS")])],"isStart":false});
            var Q6;
            Q6=makeQuery(id+"F6.opExtrude","CAP_EDGE",EDGE,{"disambiguationData":[OSD([sQuery(id+"F0.wireOp",EDGE,"E70.MirrorCS")])],"isStart":false});
            var Q7;
            Q7=makeQuery(id+"F6.opExtrude","CAP_EDGE",EDGE,{"disambiguationData":[OSD([sQuery(id+"F0.wireOp",EDGE,"E71.MirrorCS")])],"isStart":false});
            var Q8;
            Q8=makeQuery(id+"F6.opExtrude","CAP_EDGE",EDGE,{"disambiguationData":[OSD([sQuery(id+"F0.wireOp",EDGE,"E66.MirrorCS")])],"isStart":false});
            var Q9;
            Q9=makeQuery(id+"F6.opExtrude","CAP_EDGE",EDGE,{"disambiguationData":[OSD([sQuery(id+"F0.wireOp",EDGE,"E67.MirrorCS")])],"isStart":false});
            var Q10;
            Q10=makeQuery(id+"F6.opExtrude","CAP_EDGE",EDGE,{"disambiguationData":[OSD([sQuery(id+"F0.wireOp",EDGE,"E69.MirrorCS")])],"isStart":false});
            var Q11;
            Q11=makeQuery(id+"F6.opExtrude","CAP_EDGE",EDGE,{"disambiguationData":[OSD([sQuery(id+"F0.wireOp",EDGE,"E68.MirrorCS")])],"isStart":false});
            var Q12;
            Q12=makeQuery(id+"F6.opExtrude","CAP_EDGE",EDGE,{"disambiguationData":[OSD([sQuery(id+"F0.wireOp",EDGE,"E50.MirrorCS")])],"isStart":false});
            var Q13;
            Q13=makeQuery(id+"F6.opExtrude","CAP_EDGE",EDGE,{"disambiguationData":[OSD([sQuery(id+"F0.wireOp",EDGE,"E55.MirrorCS")])],"isStart":false});
            var Q14;
            Q14=makeQuery(id+"F6.opExtrude","CAP_EDGE",EDGE,{"disambiguationData":[OSD([sQuery(id+"F0.wireOp",EDGE,"E57.MirrorCS")])],"isStart":false});
            var Q15;
            Q15=makeQuery(id+"F6.opExtrude","CAP_EDGE",EDGE,{"disambiguationData":[OSD([sQuery(id+"F0.wireOp",EDGE,"E54.MirrorCS")])],"isStart":false});
            var Q16;
            Q16=makeQuery(id+"F6.opExtrude","CAP_EDGE",EDGE,{"disambiguationData":[OSD([sQuery(id+"F0.wireOp",EDGE,"E51.MirrorCS")])],"isStart":false});
            var Q17;
            Q17=makeQuery(id+"F6.opExtrude","CAP_EDGE",EDGE,{"disambiguationData":[OSD([sQuery(id+"F0.wireOp",EDGE,"E56.MirrorCS")])],"isStart":false});
            var Q18;
            Q18=makeQuery(id+"F6.opExtrude","CAP_EDGE",EDGE,{"disambiguationData":[OSD([sQuery(id+"F0.wireOp",EDGE,"E22.MirrorCS")])],"isStart":false});
            var Q19;
            Q19=makeQuery(id+"F6.opExtrude","CAP_EDGE",EDGE,{"disambiguationData":[OSD([sQuery(id+"F0.wireOp",EDGE,"E21")])],"isStart":false});
            var Q20;
            Q20=makeQuery(id+"F6.opExtrude","CAP_EDGE",EDGE,{"disambiguationData":[OSD([sQuery(id+"F0.wireOp",EDGE,"E23.2.1")])],"isStart":false});
            var Q21;
            Q21=makeQuery(id+"F6.opExtrude","CAP_EDGE",EDGE,{"disambiguationData":[OSD([sQuery(id+"F0.wireOp",EDGE,"E23.1.0")])],"isStart":false});
            var Q22;
            Q22=makeQuery(id+"F6.opExtrude","CAP_EDGE",EDGE,{"disambiguationData":[OSD([sQuery(id+"F0.wireOp",EDGE,"E23.1.1")])],"isStart":false});
            var Q23;
            Q23=makeQuery(id+"F6.opExtrude","CAP_EDGE",EDGE,{"disambiguationData":[OSD([sQuery(id+"F0.wireOp",EDGE,"E23.2.0")])],"isStart":false});
            chamfer(context, id + "F14", {"entities" : qUnion([Q0, Q1, Q2, Q3, Q4, Q5, Q6, Q7, Q8, Q9, Q10, Q11, Q12, Q13, Q14, Q15, Q16, Q17, Q18, Q19, Q20, Q21, Q22, Q23]), "width" : 1 * mm, "tangentPropagation" : true});
        }
    });
